# Revit family: NAU_Naughtone_Stnds_Hudson1
name_source: partatom
category: Furniture
revit_build: Autodesk Revit 2018 (Build: 20170223_1515(x64)
units: mm (PartAtom-declared; Revit-internal decimal feet)

## family parameters
Always vertical = Yes
Cut with Voids When Loaded = No
OmniClass Number = 23.40.20.00
OmniClass Title = General Furniture and Specialties
Room Calculation Point = No
Shared = Yes
Work Plane-Based = No

## types (1)
- NAU_Naughtone_Stnds_Hudson1
    Assembly Code = E2020200
    AssetType = Movable
    BIMObjectName = NAU_Naughtone_Stands_Hudson
    Category = Pr_40_50_84 : Stands
    Color = Various
    Description = Hudson Coatstand
    DurationUnit = year
    Finish = Oak or walnut dowels
    IfcExportAs = IfcFurnishingElementType
    IfcExportType = COATSTAND
    Keynote = Pr_40_50_84
    MainColor = Various
    ManufacturerAddress = Knaresborough Tech Park, Manse Lane, Knaresborough, HG5 8LF
    ManufacturerName = Naughtone
    ManufacturerURL = www.naughtone.com
    Material = Black or white steel supports
    Model = HUDSON
    ModelNumber = HUDSON
    ModelReference = Hudson Coatstand
    Name = Stands_Hudson_Naughtone
    NominalHeight = 1620 mm
    NominalLength = 640 mm  [stored 2.09974 ft]
    NominalWidth = 560 mm  [stored 1.83727 ft]
    ProductInformation = www.naughtone.com/products/hudson/
    Revision = 0
    Shape = Rectangular
    Size = 640 x 560 x 1620mm
    SustainabilityPerformance = FSC certified. FISP certified. ISO 14001
    URL = www.naughtone.com
    Uniclass2015Code = Pr_40_50_84
    Uniclass2015Title = Stands
    Version = 1
    WarrantyDescription = Request warranty information from naughtone
    WarrantyDurationLabor = 7
    WarrantyDurationParts = 7
    WarrantyDurationUnit = year

note: [stored X ft] marks values corroborated as IEEE doubles in the binary element streams (Revit-internal decimal feet)

## geometry (parser evidence)
native form markers: Sweep x2
no freeform markers — native parametric forms only
